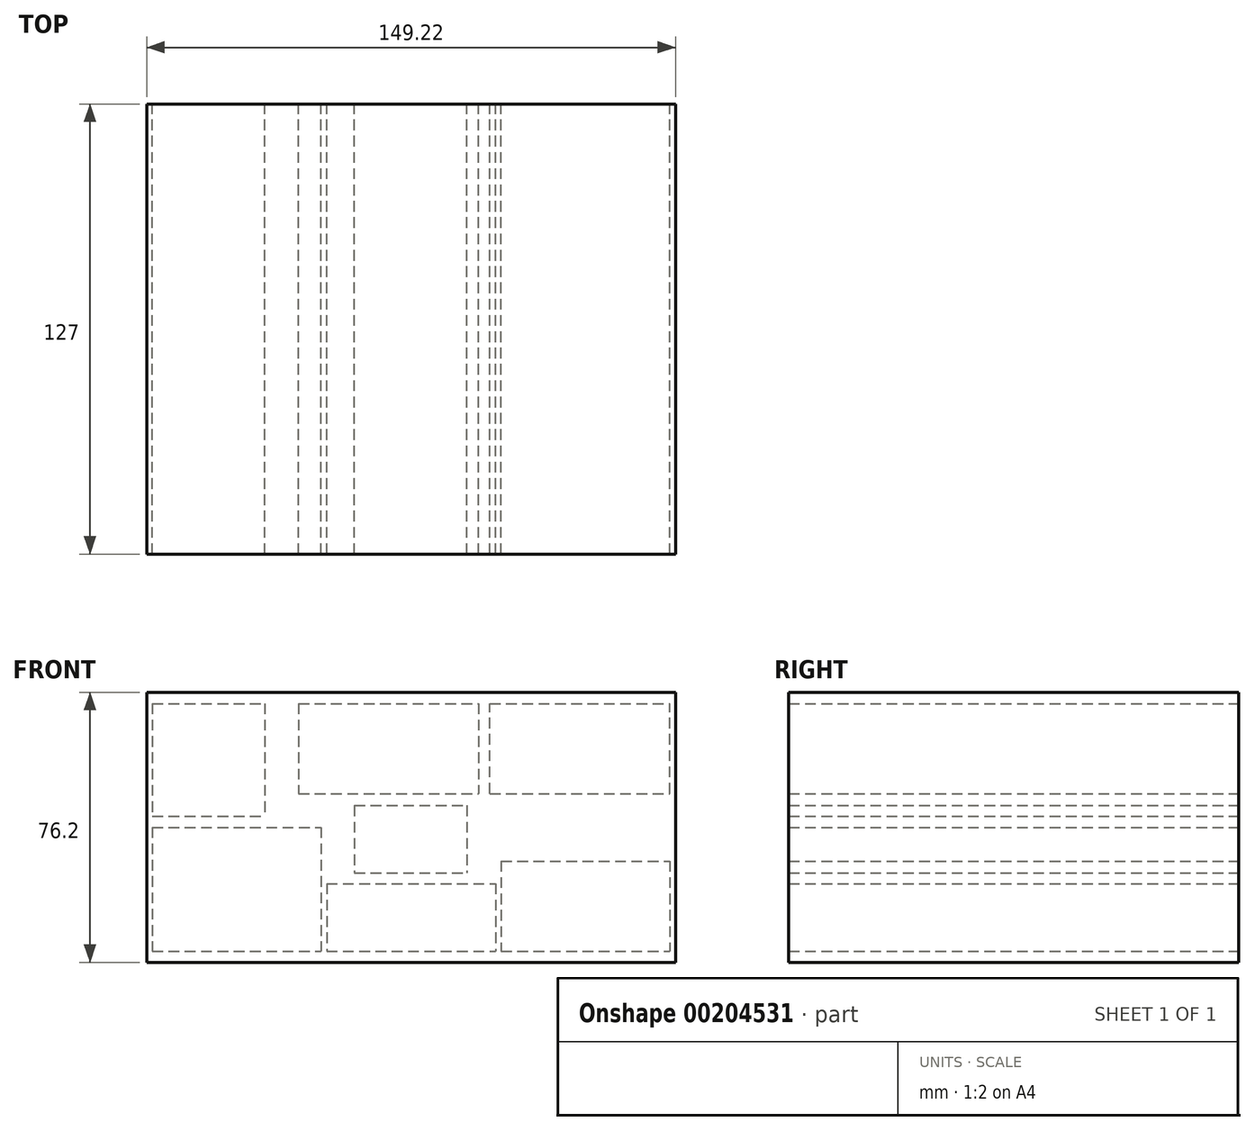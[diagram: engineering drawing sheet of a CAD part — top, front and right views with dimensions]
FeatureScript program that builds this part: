
annotation { "Feature Type Name" : "Feature", "Feature Type Description" : "" }
export const myFeature = defineFeature(function(context is Context, id is Id, definition is map)
    precondition{}
    {
        {
            var Q0;
            Q0=qCreatedBy(makeId("Front.planeOp"),FACE);
            var sketch = newSketch(context, id + "F0", { "sketchPlane" : qUnion([Q0])});
            skLineSegment(sketch, "E0.bottom", {"start": v(-93.67, 9.84) * mm, "end": v(55.55, 9.84) * mm});
            skLineSegment(sketch, "E0.top", {"start": v(-93.67, -66.36) * mm, "end": v(55.55, -66.36) * mm});
            skLineSegment(sketch, "E0.left", {"start": v(-93.67, 9.84) * mm, "end": v(-93.67, -66.36) * mm});
            skLineSegment(sketch, "E0.right", {"start": v(55.55, 9.84) * mm, "end": v(55.55, -66.36) * mm});
            skLineSegment(sketch, "E1.bottom", {"start": v(-92.08, -28.26) * mm, "end": v(-44.46, -28.26) * mm});
            skLineSegment(sketch, "E1.top", {"start": v(-92.08, -63.19) * mm, "end": v(-44.46, -63.19) * mm});
            skLineSegment(sketch, "E1.left", {"start": v(-92.08, -28.26) * mm, "end": v(-92.08, -63.19) * mm});
            skLineSegment(sketch, "E1.right", {"start": v(-44.46, -28.26) * mm, "end": v(-44.46, -63.19) * mm});
            skLineSegment(sketch, "E2.bottom", {"start": v(-42.87, -44.14) * mm, "end": v(4.75, -44.14) * mm});
            skLineSegment(sketch, "E2.top", {"start": v(-42.87, -63.19) * mm, "end": v(4.75, -63.19) * mm});
            skLineSegment(sketch, "E2.left", {"start": v(-42.87, -44.14) * mm, "end": v(-42.87, -63.19) * mm});
            skLineSegment(sketch, "E2.right", {"start": v(4.75, -44.14) * mm, "end": v(4.75, -63.19) * mm});
            skLineSegment(sketch, "E3.bottom", {"start": v(6.34, -37.79) * mm, "end": v(53.97, -37.79) * mm});
            skLineSegment(sketch, "E3.top", {"start": v(6.34, -63.19) * mm, "end": v(53.97, -63.19) * mm});
            skLineSegment(sketch, "E3.left", {"start": v(6.34, -37.79) * mm, "end": v(6.34, -63.19) * mm});
            skLineSegment(sketch, "E3.right", {"start": v(53.97, -37.79) * mm, "end": v(53.97, -63.19) * mm});
            skLineSegment(sketch, "E4.bottom", {"start": v(3.17, -18.74) * mm, "end": v(53.97, -18.74) * mm});
            skLineSegment(sketch, "E4.top", {"start": v(3.17, 6.66) * mm, "end": v(53.97, 6.66) * mm});
            skLineSegment(sketch, "E4.left", {"start": v(3.17, -18.74) * mm, "end": v(3.17, 6.66) * mm});
            skLineSegment(sketch, "E4.right", {"start": v(53.97, -18.74) * mm, "end": v(53.97, 6.66) * mm});
            skLineSegment(sketch, "E5.bottom", {"start": v(-50.8, 6.66) * mm, "end": v(0, 6.66) * mm});
            skLineSegment(sketch, "E5.top", {"start": v(-50.8, -18.74) * mm, "end": v(0, -18.74) * mm});
            skLineSegment(sketch, "E5.left", {"start": v(-50.8, 6.66) * mm, "end": v(-50.8, -18.74) * mm});
            skLineSegment(sketch, "E5.right", {"start": v(0, 6.66) * mm, "end": v(0, -18.74) * mm});
            skLineSegment(sketch, "E6.bottom", {"start": v(-92.08, 6.66) * mm, "end": v(-60.33, 6.66) * mm});
            skLineSegment(sketch, "E6.top", {"start": v(-92.08, -25.09) * mm, "end": v(-60.33, -25.09) * mm});
            skLineSegment(sketch, "E6.left", {"start": v(-92.08, 6.66) * mm, "end": v(-92.08, -25.09) * mm});
            skLineSegment(sketch, "E6.right", {"start": v(-60.33, 6.66) * mm, "end": v(-60.33, -25.09) * mm});
            skLineSegment(sketch, "E7.bottom", {"start": v(-35.08, -22.12) * mm, "end": v(-3.33, -22.12) * mm});
            skLineSegment(sketch, "E7.top", {"start": v(-35.08, -41.17) * mm, "end": v(-3.33, -41.17) * mm});
            skLineSegment(sketch, "E7.left", {"start": v(-35.08, -22.12) * mm, "end": v(-35.08, -41.17) * mm});
            skLineSegment(sketch, "E7.right", {"start": v(-3.33, -22.12) * mm, "end": v(-3.33, -41.17) * mm});
            skSolve(sketch);
        }
        {
            var Q0;
            Q0 = qSketchRegion(id + "F0", true);
            extrude(context, id + "F1", {"entities" : qUnion([Q0]), "depth" : 127 * mm});
        }
        {
            var Q0;
            Q0=makeQuery(id+"F1.opExtrude","CAP_FACE",FACE,{"disambiguationData":[OSD([sQuery(id+"F0.wireOp",EDGE,"E0.bottom"),sQuery(id+"F0.wireOp",EDGE,"E0.top"),sQuery(id+"F0.wireOp",EDGE,"E0.left"),sQuery(id+"F0.wireOp",EDGE,"E0.right"),sQuery(id+"F0.wireOp",EDGE,"E1.bottom"),sQuery(id+"F0.wireOp",EDGE,"E1.top"),sQuery(id+"F0.wireOp",EDGE,"E1.left"),sQuery(id+"F0.wireOp",EDGE,"E1.right"),sQuery(id+"F0.wireOp",EDGE,"E2.bottom"),sQuery(id+"F0.wireOp",EDGE,"E2.top"),sQuery(id+"F0.wireOp",EDGE,"E2.left"),sQuery(id+"F0.wireOp",EDGE,"E2.right"),sQuery(id+"F0.wireOp",EDGE,"E3.bottom"),sQuery(id+"F0.wireOp",EDGE,"E3.top"),sQuery(id+"F0.wireOp",EDGE,"E3.left"),sQuery(id+"F0.wireOp",EDGE,"E3.right"),sQuery(id+"F0.wireOp",EDGE,"E4.bottom"),sQuery(id+"F0.wireOp",EDGE,"E4.top"),sQuery(id+"F0.wireOp",EDGE,"E4.left"),sQuery(id+"F0.wireOp",EDGE,"E4.right"),sQuery(id+"F0.wireOp",EDGE,"E5.bottom"),sQuery(id+"F0.wireOp",EDGE,"E5.top"),sQuery(id+"F0.wireOp",EDGE,"E5.left"),sQuery(id+"F0.wireOp",EDGE,"E5.right"),sQuery(id+"F0.wireOp",EDGE,"E6.bottom"),sQuery(id+"F0.wireOp",EDGE,"E6.top"),sQuery(id+"F0.wireOp",EDGE,"E6.left"),sQuery(id+"F0.wireOp",EDGE,"E6.right"),sQuery(id+"F0.wireOp",EDGE,"E7.bottom"),sQuery(id+"F0.wireOp",EDGE,"E7.top"),sQuery(id+"F0.wireOp",EDGE,"E7.left"),sQuery(id+"F0.wireOp",EDGE,"E7.right")])],"isStart":false});
            var sketch = newSketch(context, id + "F2", { "sketchPlane" : qUnion([Q0])});
            skLineSegment(sketch, "E8.bottom", {"start": v(-93.67, 9.84) * mm, "end": v(55.55, 9.84) * mm});
            skLineSegment(sketch, "E8.top", {"start": v(-93.67, -66.36) * mm, "end": v(55.55, -66.36) * mm});
            skLineSegment(sketch, "E8.left", {"start": v(-93.67, 9.84) * mm, "end": v(-93.67, -66.36) * mm});
            skLineSegment(sketch, "E8.right", {"start": v(55.55, 9.84) * mm, "end": v(55.55, -66.36) * mm});
            skSolve(sketch);
        }
        {
            var Q0;
            Q0 = qSketchRegion(id + "F2", true);
            extrude(context, id + "F3", {"entities" : qUnion([Q0]), "operationType" : NewBodyOperationType.ADD, "depth" : 1 / 203.2 * mm});
        }
    });
